# Revit family: LAMP_TRACE 100 IP65
name_source: partatom
category: Modelos genéricos
revit_build: Autodesk Revit 2015 (Build: 20140606_1530(x64)
units: mm (PartAtom-declared; Revit-internal decimal feet)

## types (1)
- 68LM 3000 BLACK
    CRI = 80
    Descripción = TRACE IP65 100 HOR 70 WW BK.
    Dimensions = 105 x 101 x 105
    Efficacy = 27 lm/W
    Elevación por defecto = 1219 mm
    Fabricante = LAMP
    Finish = Cataphoresis
    Gear = Electronic
    IEE = A++
    Initial color = 3000 K
    Initial intensity = 68 lm
    Installation instructions = https://www.lamp.es
    Insulation class = I
    LED Lifetime = 100.000 L90 B10
    Lamp = MID-POWER LED
    Last update = 13/11/2020
    Luminaire type = Outdoor - Wall Mounted
    MacAdam = <3
    Manufacturer URL = http://www.lamp.es
    Manufacturer country = Spain
    Manufacturer name = LAMP
    Modelo = TC110H0165SY830NB
    Photometric web file = Cuerpo Trace 100 : 68LM 3000 BLACK
    Plum = 3 W
    Power = 1 W
    Power Supply = 100-240V 50-60Hz
    Product URL = https://www.lamp.es
    Product code = TC110H0165SY830NB
    Product datasheet = http://www.lamp.es
    Protection rating = IP65 / IK07
    Recessed dimensions = 107 x 135 x 112
    Type = MID POWER OSRAM
    Weight = 0.67 kg
